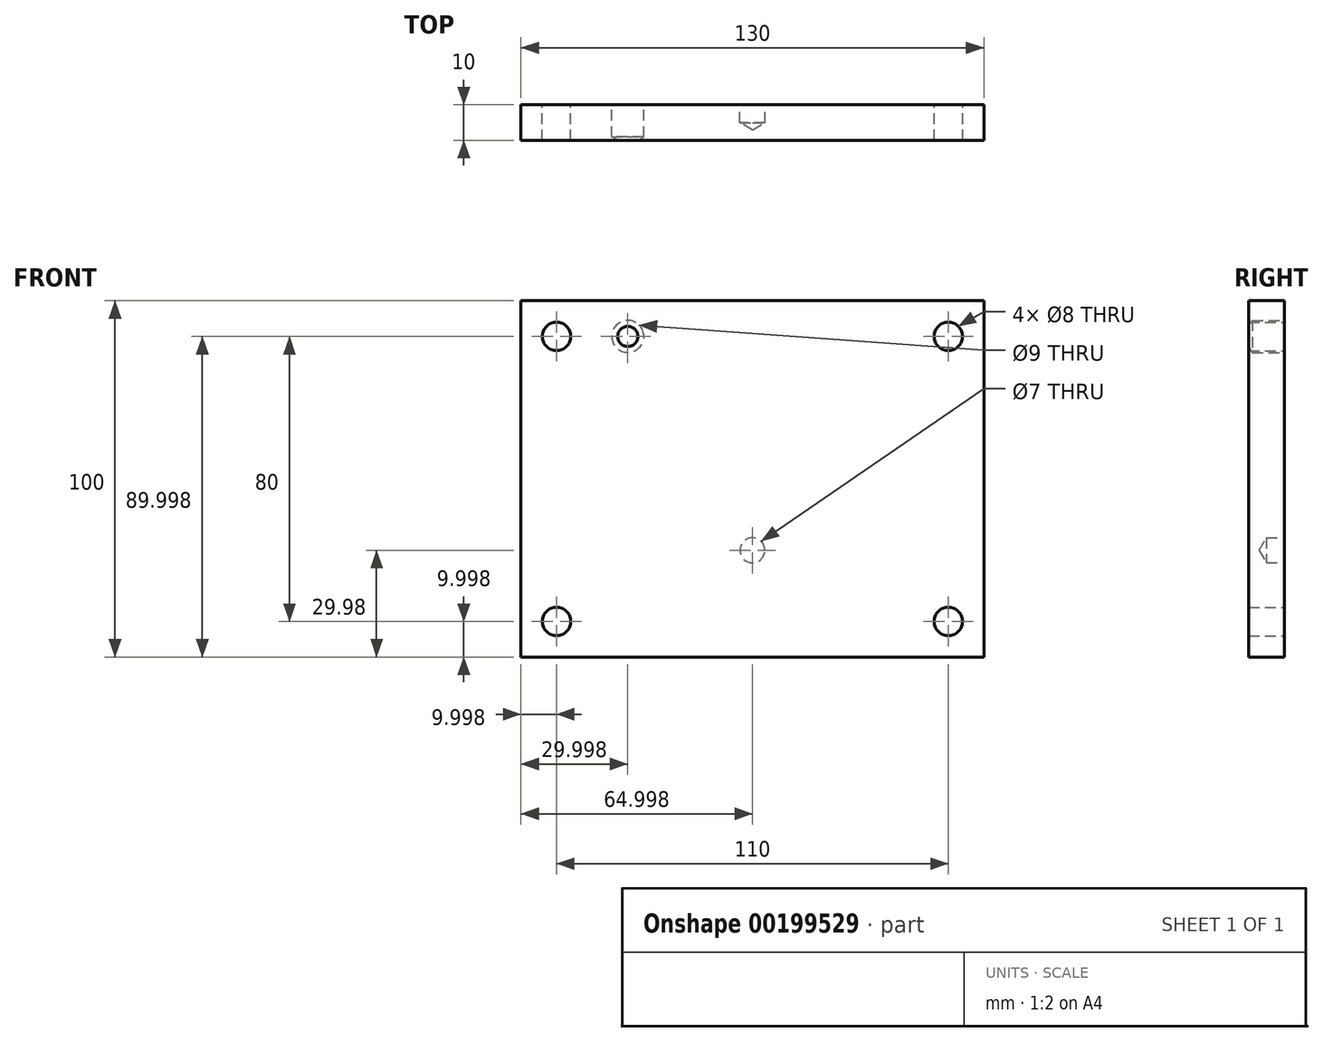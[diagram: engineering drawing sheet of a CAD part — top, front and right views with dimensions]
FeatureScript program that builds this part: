
annotation { "Feature Type Name" : "Feature", "Feature Type Description" : "" }
export const myFeature = defineFeature(function(context is Context, id is Id, definition is map)
    precondition{}
    {
        {
            var Q0;
            Q0=qCreatedBy(makeId("Front.planeOp"),FACE);
            var sketch = newSketch(context, id + "F0", { "sketchPlane" : qUnion([Q0])});
            skLineSegment(sketch, "E0.bottom", {"start": v(-74.06, 70.02) * mm, "end": v(55.94, 70.02) * mm});
            skLineSegment(sketch, "E0.top", {"start": v(-74.06, -29.98) * mm, "end": v(55.94, -29.98) * mm});
            skLineSegment(sketch, "E0.left", {"start": v(-74.06, 70.02) * mm, "end": v(-74.06, -29.98) * mm});
            skLineSegment(sketch, "E0.right", {"start": v(55.94, 70.02) * mm, "end": v(55.94, -29.98) * mm});
            skSolve(sketch);
        }
        {
            var Q0;
            Q0=makeQuery(id+"F0.imprint","IMPRINT",FACE,{"disambiguationData":[TD([[makeQuery(id+"F0.imprint","IMPRINT",EDGE,{"derivedFrom":sQuery(id+"F0.wireOp",EDGE,"E0.bottom")}),-1.0]])]});
            extrude(context, id + "F1", {"entities" : qUnion([Q0]), "depth" : 10 * mm});
        }
        {
            var Q0;
            Q0=makeQuery(id+"F1.opExtrude","CAP_FACE",FACE,{"disambiguationData":[OSD([sQuery(id+"F0.wireOp",EDGE,"E0.bottom"),sQuery(id+"F0.wireOp",EDGE,"E0.top"),sQuery(id+"F0.wireOp",EDGE,"E0.left"),sQuery(id+"F0.wireOp",EDGE,"E0.right")])],"isStart":true});
            var sketch = newSketch(context, id + "F2", { "sketchPlane" : qUnion([Q0])});
            skCircle(sketch, "E1", {"center": v(44.06, 60.02) * mm, "radius": 4.5 * mm});
            skCircle(sketch, "E2", {"center": v(-45.94, 60.02) * mm, "radius": 4 * mm});
            skCircle(sketch, "E3", {"center": v(-45.94, -19.98) * mm, "radius": 4 * mm});
            skCircle(sketch, "E4", {"center": v(64.06, -19.98) * mm, "radius": 4 * mm});
            skCircle(sketch, "E5", {"center": v(64.06, 60.02) * mm, "radius": 4 * mm});
            skCircle(sketch, "E6", {"center": v(44.06, 0.02) * mm, "radius": 3.5 * mm});
            skCircle(sketch, "E7", {"center": v(44.06, -19.98) * mm, "radius": 3.5 * mm});
            skCircle(sketch, "E8", {"center": v(9.06, 60.18) * mm, "radius": 4.5 * mm});
            skCircle(sketch, "E9", {"center": v(-25.94, 60.02) * mm, "radius": 4.5 * mm});
            skCircle(sketch, "E10", {"center": v(9.06, 0) * mm, "radius": 3.5 * mm});
            skCircle(sketch, "E11", {"center": v(9.06, -18.94) * mm, "radius": 3.5 * mm});
            skCircle(sketch, "E12", {"center": v(-25.94, 0.02) * mm, "radius": 3.5 * mm});
            skCircle(sketch, "E13", {"center": v(-25.94, -19.98) * mm, "radius": 3.5 * mm});
            skSolve(sketch);
        }
        {
            var Q0;
            Q0=sQuery(id+"F2.wireOp",VERTEX,"E1.center");
            var Q1;
            Q1=makeQuery(id+"F1.opExtrude","SWEPT_BODY",BODY,{"disambiguationData":[OSD([sQuery(id+"F0.wireOp",EDGE,"E0.bottom"),sQuery(id+"F0.wireOp",EDGE,"E0.top"),sQuery(id+"F0.wireOp",EDGE,"E0.left"),sQuery(id+"F0.wireOp",EDGE,"E0.right")])]});
            hole(context, id + "F3", {"style" : HoleStyle.SIMPLE, "endStyle" : HoleEndStyle.BLIND, "holeDiameter" : 9 * mm, "holeDepth" : 9 * mm, "locations" : qUnion([Q0]), "scope" : qUnion([Q1])});
        }
        {
            var Q0;
            Q0=makeQuery(id+"F2.imprint","IMPRINT",FACE,{"disambiguationData":[TD([[makeQuery(id+"F2.imprint","IMPRINT",EDGE,{"derivedFrom":sQuery(id+"F2.wireOp",EDGE,"E3")}),1.0]])]});
            var Q1;
            Q1=sQuery(id+"F2.wireOp",EDGE,"E3");
            extrude(context, id + "F4", {"entities" : qUnion([Q0]), "operationType" : NewBodyOperationType.REMOVE, "surfaceEntities" : qUnion([Q1]), "oppositeDirection" : true, "depth" : 25 * mm});
        }
        {
            var Q0;
            Q0=makeQuery(id+"F2.imprint","IMPRINT",FACE,{"disambiguationData":[TD([[makeQuery(id+"F2.imprint","IMPRINT",EDGE,{"derivedFrom":sQuery(id+"F2.wireOp",EDGE,"E4")}),1.0]])]});
            var Q1;
            Q1=sQuery(id+"F2.wireOp",EDGE,"E4");
            extrude(context, id + "F5", {"entities" : qUnion([Q0]), "operationType" : NewBodyOperationType.REMOVE, "surfaceEntities" : qUnion([Q1]), "oppositeDirection" : true, "depth" : 25 * mm});
        }
        {
            var Q0;
            Q0=makeQuery(id+"F2.imprint","IMPRINT",FACE,{"disambiguationData":[TD([[makeQuery(id+"F2.imprint","IMPRINT",EDGE,{"derivedFrom":sQuery(id+"F2.wireOp",EDGE,"E5")}),1.0]])]});
            extrude(context, id + "F6", {"entities" : qUnion([Q0]), "operationType" : NewBodyOperationType.REMOVE, "oppositeDirection" : true, "depth" : 25 * mm});
        }
        {
            var Q0;
            Q0=makeQuery(id+"F2.imprint","IMPRINT",FACE,{"disambiguationData":[TD([[makeQuery(id+"F2.imprint","IMPRINT",EDGE,{"derivedFrom":sQuery(id+"F2.wireOp",EDGE,"E2")}),1.0]])]});
            extrude(context, id + "F7", {"entities" : qUnion([Q0]), "operationType" : NewBodyOperationType.REMOVE, "oppositeDirection" : true, "depth" : 25 * mm});
        }
        {
            var Q0;
            Q0=sQuery(id+"F2.wireOp",VERTEX,"E10.center");
            var Q1;
            Q1=makeQuery(id+"F1.opExtrude","SWEPT_BODY",BODY,{"disambiguationData":[OSD([sQuery(id+"F0.wireOp",EDGE,"E0.bottom"),sQuery(id+"F0.wireOp",EDGE,"E0.top"),sQuery(id+"F0.wireOp",EDGE,"E0.left"),sQuery(id+"F0.wireOp",EDGE,"E0.right")])]});
            hole(context, id + "F8", {"style" : HoleStyle.SIMPLE, "endStyle" : HoleEndStyle.BLIND, "holeDiameter" : 7 * mm, "holeDepth" : 5 * mm, "locations" : qUnion([Q0]), "scope" : qUnion([Q1])});
        }
    });
